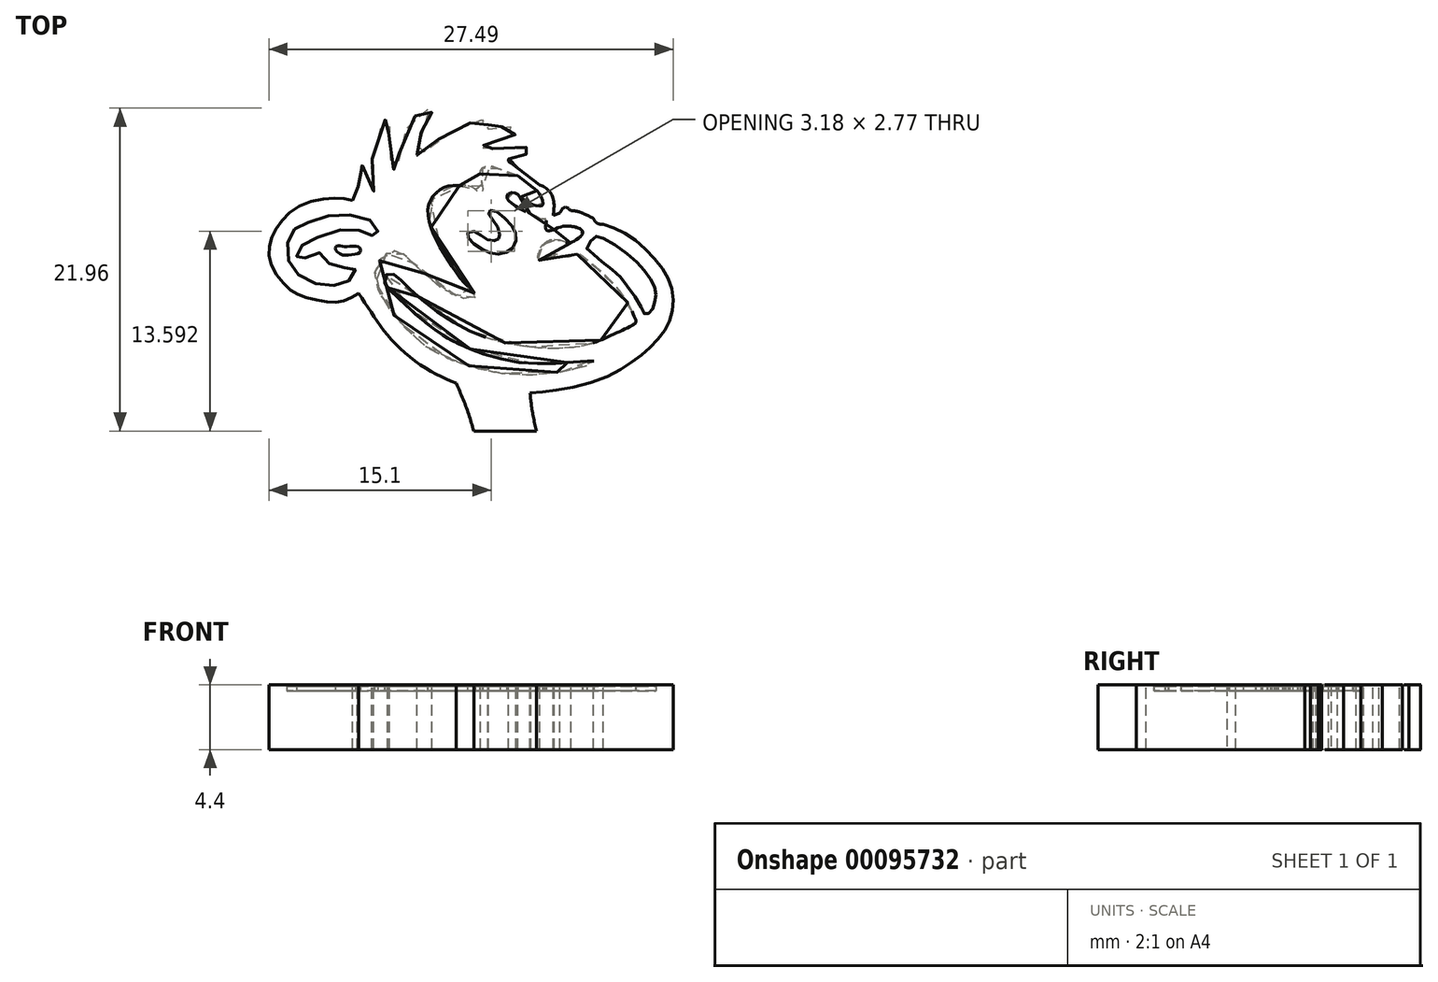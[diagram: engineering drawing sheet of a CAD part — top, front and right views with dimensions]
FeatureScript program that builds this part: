
annotation { "Feature Type Name" : "Feature", "Feature Type Description" : "" }
export const myFeature = defineFeature(function(context is Context, id is Id, definition is map)
    precondition{}
    {
        {
            var Q0;
            Q0=qCreatedBy(makeId("Top.planeOp"),FACE);
            var sketch = newSketch(context, id + "F0", { "sketchPlane" : qUnion([Q0])});
            skPoint(sketch, "E0", {"position": v(0, 11.87) * mm});
            skPoint(sketch, "E1", {"position": v(15, 0) * mm});
            skFitSpline(sketch, "E2", {"points": [v(-8.12, 3.82) * mm, v(-9.48, 3.97) * mm, v(-11.73, 3.42) * mm, v(-13.2, 2.1) * mm, v(-13.76, 0.83) * mm, v(-13.63, -0.62) * mm, v(-12.54, -2.1) * mm, v(-11.49, -2.72) * mm, v(-9.85, -3.08) * mm, v(-8.7, -3.03) * mm, v(-7.7, -2.5) * mm], "startDerivative": vector(-13.17, 2.57) * mm, "endDerivative": vector(11.4, 7.36) * mm});
            skFitSpline(sketch, "E3", {"points": [v(-7.7, -2.5) * mm, v(-6.54, -4.27) * mm, v(-5.13, -6.01) * mm, v(-2.97, -7.7) * mm, v(-1.1, -8.61) * mm], "startDerivative": vector(4.78, -7.41) * mm, "endDerivative": vector(7.74, -3.25) * mm});
            skFitSpline(sketch, "E4", {"points": [v(-1.1, -8.61) * mm, v(-0.4, -10.23) * mm, v(0.12, -11.87) * mm], "startDerivative": vector(1.47, -3.2) * mm, "endDerivative": vector(0.95, -3.33) * mm});
            skFitSpline(sketch, "E5", {"points": [v(4.37, -11.87) * mm, v(4.07, -10.32) * mm, v(3.95, -9.28) * mm], "startDerivative": vector(-0.62, 2.95) * mm, "endDerivative": vector(-0.2, 2.21) * mm});
            skFitSpline(sketch, "E6", {"points": [v(3.95, -9.28) * mm, v(5.76, -9.1) * mm, v(8.93, -8.27) * mm, v(10.86, -7.18) * mm, v(11.98, -6.32) * mm, v(12.9, -5.3) * mm, v(13.48, -4.27) * mm, v(13.68, -3.1) * mm, v(13.49, -1.84) * mm, v(12.83, -0.68) * mm, v(11.6, 0.67) * mm, v(10.23, 1.68) * mm, v(8.93, 2.18) * mm], "startDerivative": vector(18.7, 1.3) * mm, "endDerivative": vector(-16.92, 5.51) * mm});
            skFitSpline(sketch, "E7", {"points": [v(8.93, 2.18) * mm, v(8.5, 2.27) * mm, v(8.26, 2.58) * mm], "startDerivative": vector(-0.94, 0.04) * mm, "endDerivative": vector(-0.38, 0.76) * mm});
            skFitSpline(sketch, "E8", {"points": [v(8.26, 2.58) * mm, v(7.22, 3.06) * mm, v(6.74, 3.1) * mm], "startDerivative": vector(-1.86, 1) * mm, "endDerivative": vector(-1.14, -0.03) * mm});
            skFitSpline(sketch, "E9", {"points": [v(6.74, 3.1) * mm, v(6.35, 3.35) * mm, v(6.1, 3.18) * mm, v(5.97, 2.96) * mm], "startDerivative": vector(-1.01, 0.96) * mm, "endDerivative": vector(-0.39, -0.73) * mm});
            skFitSpline(sketch, "E10", {"points": [v(5.97, 2.96) * mm, v(5.51, 2.78) * mm], "startDerivative": vector(-0.46, -0.19) * mm, "endDerivative": vector(-0.46, -0.19) * mm});
            skFitSpline(sketch, "E11", {"points": [v(-8.12, 3.82) * mm, v(-7.82, 3.82) * mm, v(-7.7, 4.03) * mm, v(-7.8, 5.63) * mm, v(-7.58, 6.19) * mm, v(-7.4, 6.1) * mm, v(-6.71, 4.43) * mm, v(-6.7, 4.76) * mm, v(-6.74, 7.07) * mm, v(-5.85, 9.33) * mm, v(-5.67, 9.28) * mm, v(-5.61, 8.9) * mm, v(-5.73, 7.67) * mm, v(-5.18, 5.68) * mm, v(-5.05, 6.2) * mm, v(-4.56, 8.48) * mm, v(-3.18, 10.07) * mm, v(-2.77, 9.96) * mm, v(-2.75, 9.72) * mm, v(-3.18, 9.1) * mm, v(-3.58, 8) * mm, v(-3.74, 7.07) * mm, v(-3.69, 6.83) * mm, v(-2.67, 7.66) * mm, v(-0.95, 8.7) * mm, v(0.71, 9.3) * mm, v(1.09, 9.14) * mm, v(1.09, 8.78) * mm, v(1.13, 8.65) * mm, v(1.64, 8.74) * mm, v(2.77, 8.75) * mm, v(3, 8.4) * mm, v(2.84, 8.23) * mm, v(0.87, 7.6) * mm, v(0.56, 7.33) * mm, v(0.7, 7.25) * mm, v(1.9, 7.4) * mm, v(3.72, 7.4) * mm, v(3.96, 7.24) * mm, v(3.97, 7.03) * mm, v(3.82, 6.96) * mm, v(3.3, 6.9) * mm, v(2.66, 6.75) * mm, v(2.49, 6.62) * mm, v(2.5, 6.46) * mm, v(2.7, 6.32) * mm, v(3.1, 5.99) * mm, v(3.23, 5.73) * mm, v(3.14, 5.5) * mm, v(2.84, 5.53) * mm, v(2.16, 5.8) * mm, v(1.5, 6.09) * mm, v(0.95, 6.11) * mm, v(0.57, 5.87) * mm, v(0.6, 5.33) * mm, v(0.7, 4.8) * mm, v(0.7, 4.4) * mm, v(0.47, 4.37) * mm, v(0.09, 4.68) * mm, v(-0.68, 4.82) * mm, v(-1.68, 4.77) * mm, v(-2.53, 4.24) * mm, v(-2.98, 3.37) * mm, v(-2.74, 1.83) * mm, v(-1.6, -0.31) * mm, v(-0.4, -1.94) * mm, v(0.13, -2.47) * mm, v(0.23, -2.77) * mm, v(0.1, -2.94) * mm, v(-1.24, -2.63) * mm, v(-2.88, -1.5) * mm, v(-4.25, -0.22) * mm, v(-4.8, 0.25) * mm, v(-5.17, 0.37) * mm, v(-5.92, 0.14) * mm, v(-6.44, -0.56) * mm, v(-6.63, -1.17) * mm, v(-6.52, -1.95) * mm, v(-5.86, -3.22) * mm, v(-4.69, -4.7) * mm, v(-2.88, -6.31) * mm, v(-0.39, -7.38) * mm, v(1.46, -7.85) * mm, v(3.9, -8.05) * mm, v(6.6, -7.73) * mm, v(8.12, -7.28) * mm, v(8.3, -7.11) * mm, v(7.95, -7.1) * mm, v(5.96, -7.26) * mm, v(3, -7.17) * mm, v(0.22, -6.42) * mm, v(-2.59, -4.94) * mm, v(-5.35, -2.52) * mm, v(-5.9, -1.83) * mm, v(-5.84, -1.26) * mm, v(-5.41, -1.16) * mm, v(-4.79, -1.67) * mm, v(-3.47, -2.9) * mm, v(-0.76, -4.75) * mm, v(1.6, -5.7) * mm, v(4.76, -6.2) * mm, v(7.66, -6.04) * mm, v(9.29, -5.44) * mm, v(10.62, -4.83) * mm, v(11.13, -4.5) * mm, v(11.08, -4.17) * mm, v(10.3, -2.68) * mm, v(8.37, -0.7) * mm, v(7.46, 0) * mm, v(7.34, 0.15) * mm, v(7.12, 0.13) * mm, v(6.43, -0.06) * mm, v(5.93, 0.06) * mm, v(5.52, 0.18) * mm, v(4.98, -0.13) * mm, v(4.7, -0.34) * mm, v(4.5, -0.13) * mm, v(4.57, 0.48) * mm, v(5.17, 1.07) * mm, v(5.86, 1.16) * mm, v(6.54, 0.91) * mm, v(6.74, 0.95) * mm, v(7.5, 1.49) * mm, v(7.4, 1.84) * mm, v(6.76, 2.05) * mm, v(6.04, 2.02) * mm, v(5.46, 1.79) * mm, v(5.16, 1.73) * mm, v(5, 1.87) * mm, v(5.05, 2.36) * mm, v(5.03, 2.55) * mm, v(4.7, 2.55) * mm, v(4.34, 2.73) * mm, v(3.08, 3.33) * mm, v(2.5, 3.82) * mm, v(2.37, 4.06) * mm, v(2.56, 4.3) * mm, v(3, 4.3) * mm, v(3.3, 4.02) * mm, v(3.84, 3.69) * mm, v(4.3, 3.46) * mm, v(4.73, 3.45) * mm, v(4.83, 3.56) * mm, v(4.7, 4.06) * mm, v(4.4, 4.52) * mm, v(4.38, 4.72) * mm, v(4.61, 4.84) * mm, v(5.05, 4.63) * mm, v(5.38, 4.28) * mm, v(5.57, 3.58) * mm, v(5.51, 2.78) * mm], "startDerivative": vector(81.73, -10.1) * mm, "endDerivative": vector(-18.64, -120.3) * mm});
            skFitSpline(sketch, "E12", {"points": [v(1.82, 1.2) * mm, v(1.9, 1.36) * mm, v(1.68, 2.11) * mm, v(1.17, 2.78) * mm, v(1.16, 3.08) * mm, v(1.52, 3.12) * mm, v(2.5, 2.32) * mm, v(2.97, 1.54) * mm, v(2.87, 0.74) * mm, v(2.26, 0.24) * mm, v(1.35, 0.2) * mm, v(0.44, 0.66) * mm, v(-0.26, 1.26) * mm, v(-0.26, 1.63) * mm, v(0.2, 1.68) * mm, v(0.9, 1.22) * mm, v(1.54, 1.07) * mm, v(1.82, 1.2) * mm]});
            skFitSpline(sketch, "E13", {"points": [v(10.55, -2) * mm, v(9.7, -1) * mm, v(8.38, 0) * mm, v(8.05, 0.37) * mm, v(7.82, 0.43) * mm, v(7.87, 0.73) * mm, v(8.35, 1.34) * mm, v(8.8, 1.29) * mm, v(10.56, 0.18) * mm, v(11.69, -0.94) * mm, v(12.3, -1.82) * mm, v(12.52, -2.55) * mm, v(12.41, -3.17) * mm, v(12.26, -3.63) * mm, v(11.98, -3.89) * mm, v(11.75, -3.92) * mm, v(11.5, -3.43) * mm, v(10.55, -2) * mm]});
            skLineSegment(sketch, "E14", {"start": v(0.12, -11.87) * mm, "end": v(4.37, -11.87) * mm});
            skFitSpline(sketch, "E15", {"points": [v(-8.95, 1.8) * mm, v(-7.56, 1.76) * mm, v(-6.8, 1.45) * mm, v(-6.58, 1.38) * mm, v(-6.4, 1.75) * mm, v(-6.79, 2.37) * mm, v(-8.46, 2.83) * mm, v(-10.32, 2.63) * mm, v(-11.72, 2.05) * mm, v(-12.22, 1.69) * mm, v(-12.6, 0.52) * mm, v(-12.3, -0.7) * mm, v(-11.3, -1.56) * mm, v(-9.82, -2) * mm, v(-8.73, -1.78) * mm, v(-8.02, -1.35) * mm, v(-8, -0.76) * mm, v(-8.62, -0.77) * mm, v(-9.64, -0.54) * mm, v(-10.28, 0.24) * mm, v(-11.15, 0) * mm, v(-11.67, -0.17) * mm, v(-11.93, 0) * mm, v(-11.73, 0.6) * mm, v(-11.02, 1.08) * mm, v(-8.95, 1.8) * mm]});
            skFitSpline(sketch, "E16", {"points": [v(-8.32, 0.68) * mm, v(-7.7, 0.64) * mm, v(-7.6, 0.3) * mm, v(-8.2, 0.12) * mm, v(-8.9, 0.14) * mm, v(-9.3, 0.53) * mm, v(-9.16, 0.72) * mm, v(-8.8, 0.68) * mm, v(-8.32, 0.68) * mm]});
            skLineSegment(sketch, "E17", {"start": v(4.61, 4.84) * mm, "end": v(3.1, 5.99) * mm});
            skLineSegment(sketch, "E18", {"start": v(3.1, 5.48) * mm, "end": v(4.43, 4.48) * mm});
            skSolve(sketch);
        }
        {
            var Q0;
            Q0 = qSketchRegion(id + "F0", true);
            var Q1;
            Q1=makeQuery(id+"F0.imprint","IMPRINT",FACE,{"disambiguationData":[TD([[makeQuery(id+"F0.imprint","IMPRINT",EDGE,{"derivedFrom":sQuery(id+"F0.wireOp",EDGE,"E12")}),1.0]])]});
            var Q2;
            Q2=makeQuery(id+"F0.imprint","IMPRINT",FACE,{"disambiguationData":[TD([[makeQuery(id+"F0.imprint","IMPRINT",EDGE,{"derivedFrom":sQuery(id+"F0.wireOp",EDGE,"E12")}),-1.0]])]});
            var Q3;
            Q3=makeQuery(id+"F0.imprint","IMPRINT",FACE,{"disambiguationData":[TD([[makeQuery(id+"F0.imprint","IMPRINT",EDGE,{"derivedFrom":sQuery(id+"F0.wireOp",EDGE,"E15")}),1.0]])]});
            var Q4;
            Q4=makeQuery(id+"F0.imprint","IMPRINT",FACE,{"disambiguationData":[TD([[makeQuery(id+"F0.imprint","IMPRINT",EDGE,{"derivedFrom":sQuery(id+"F0.wireOp",EDGE,"E16")}),-1.0]])]});
            var Q5;
            Q5=makeQuery(id+"F0.imprint","IMPRINT",FACE,{"disambiguationData":[TD([[makeQuery(id+"F0.imprint","IMPRINT",EDGE,{"derivedFrom":sQuery(id+"F0.wireOp",EDGE,"E13")}),-1.0]])]});
            extrude(context, id + "F1", {"entities" : qUnion([Q0, Q1, Q2, Q3, Q4, Q5]), "oppositeDirection" : true, "depth" : 4 * mm});
        }
        {
            var Q0;
            {var subQ0=sQuery(id+"F0.wireOp",EDGE,"E2");Q0=makeQuery(id+"F0.imprint","IMPRINT",FACE,{"disambiguationData":[TD([[makeQuery(id+"F0.imprint","IMPRINT",EDGE,{"derivedFrom":subQ0}),1.0]])]});}
            var Q1;
            Q1=makeQuery(id+"F0.imprint","IMPRINT",FACE,{"disambiguationData":[TD([[makeQuery(id+"F0.imprint","IMPRINT",EDGE,{"derivedFrom":sQuery(id+"F0.wireOp",EDGE,"E12")}),-1.0]])]});
            var Q2;
            {var subQ0=sQuery(id+"F0.wireOp",EDGE,"E17");Q2=makeQuery(id+"F0.imprint","IMPRINT",FACE,{"disambiguationData":[TD([[makeQuery(id+"F0.imprint","IMPRINT",EDGE,{"derivedFrom":subQ0}),1.0]])]});}
            extrude(context, id + "F2", {"entities" : qUnion([Q0, Q1, Q2]), "operationType" : NewBodyOperationType.ADD, "depth" : 0.4 * mm});
        }
        {
            var Q0;
            Q0=makeQuery(id+"F0.imprint","IMPRINT",FACE,{"disambiguationData":[TD([[makeQuery(id+"F0.imprint","IMPRINT",EDGE,{"derivedFrom":sQuery(id+"F0.wireOp",EDGE,"E15")}),1.0]])]});
            var Q1;
            Q1=makeQuery(id+"F0.imprint","IMPRINT",FACE,{"disambiguationData":[TD([[makeQuery(id+"F0.imprint","IMPRINT",EDGE,{"derivedFrom":sQuery(id+"F0.wireOp",EDGE,"E16")}),-1.0]])]});
            var Q2;
            {var subQ0=sQuery(id+"F0.wireOp",EDGE,"e1678d52-f086-40c0-a34f-b6ecca3570dc");Q2=makeQuery(id+"F0.imprint","IMPRINT",FACE,{"disambiguationData":[TD([[makeQuery(id+"F0.imprint","IMPRINT",EDGE,{"derivedFrom":subQ0}),-1.0]])]});}
            var Q3;
            Q3=makeQuery(id+"F0.imprint","IMPRINT",FACE,{"disambiguationData":[TD([[makeQuery(id+"F0.imprint","IMPRINT",EDGE,{"derivedFrom":sQuery(id+"F0.wireOp",EDGE,"E13")}),-1.0]])]});
            var Q4;
            Q4=makeQuery(id+"F0.imprint","IMPRINT",FACE,{"disambiguationData":[TD([[makeQuery(id+"F0.imprint","IMPRINT",EDGE,{"derivedFrom":sQuery(id+"F0.wireOp",EDGE,"E12")}),1.0]])]});
            extrude(context, id + "F3", {"entities" : qUnion([Q0, Q1, Q2, Q3, Q4]), "depth" : 0.3 * mm});
        }
    });
